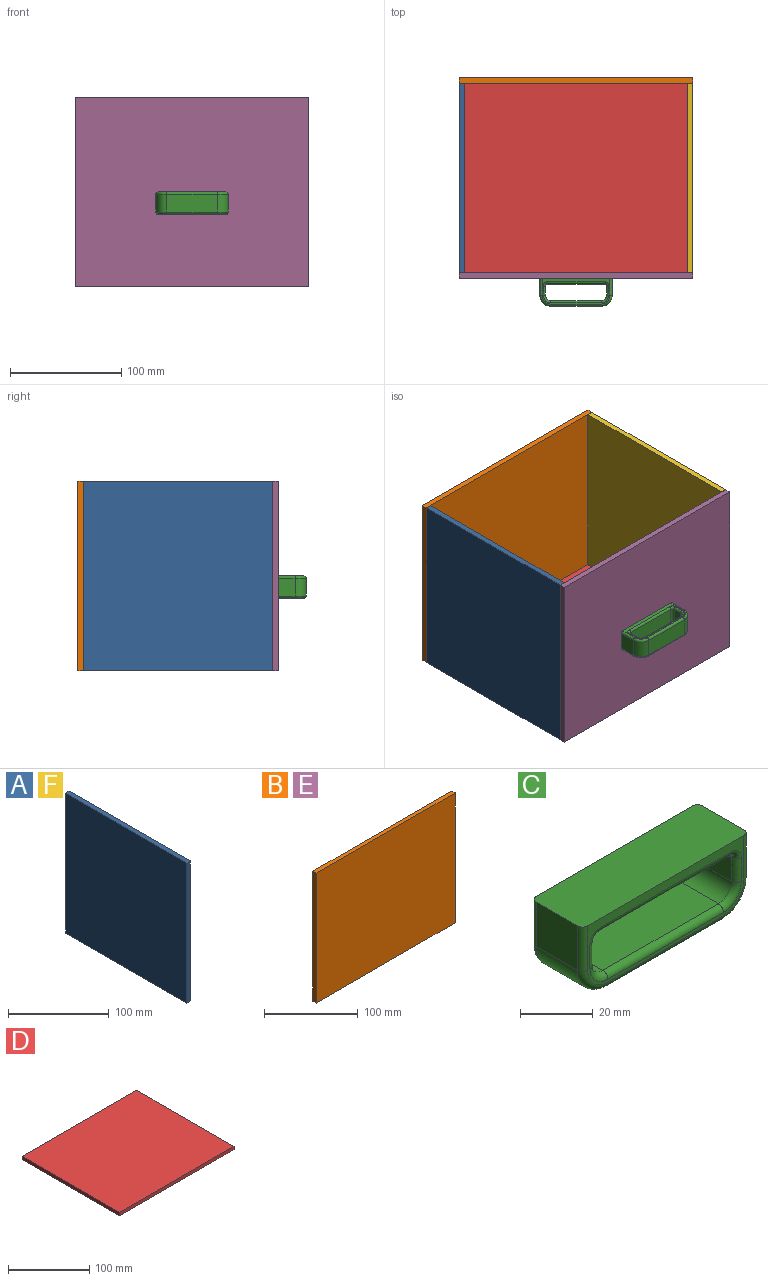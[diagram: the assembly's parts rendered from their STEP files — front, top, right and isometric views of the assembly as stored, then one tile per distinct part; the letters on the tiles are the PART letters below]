
ASSEMBLY  parts=6 mates=13
PART A: 6 faces, bbox 5x170x170 mm
  f0: plane 170x5mm, normal (0,0,1), area 850mm2, adj f1,f3,f4,f5
  f1: plane 170x5mm, normal (0,-1,0), area 850mm2, adj f0,f2,f4,f5
  f2: plane 170x5mm, normal (0,0,-1), area 850mm2, adj f1,f3,f4,f5
  f3: plane 170x5mm, normal (0,1,0), area 850mm2, adj f0,f2,f4,f5
  f4: plane 170x170mm, normal (1,0,0), area 28900mm2, adj f0,f1,f2,f3
  f5: plane 170x170mm, normal (-1,0,0), area 28900mm2, adj f0,f1,f2,f3
PART B: 6 faces, bbox 210x5x170 mm
  f0: plane 210x5mm, normal (0,0,1), area 1050mm2, adj f1,f3,f4,f5
  f1: plane 170x5mm, normal (-1,0,0), area 850mm2, adj f0,f2,f4,f5
  f2: plane 210x5mm, normal (0,0,-1), area 1050mm2, adj f1,f3,f4,f5
  f3: plane 170x5mm, normal (1,0,0), area 850mm2, adj f0,f2,f4,f5
  f4: plane 210x170mm, normal (0,-1,0), area 35700mm2, adj f0,f1,f2,f3
  f5: plane 210x170mm, normal (0,1,0), area 35700mm2, adj f0,f1,f2,f3
PART C: 42 faces, bbox 66.6x20x25.8 mm
  f0: plane 61x23mm, normal (0,1,0), area 282.4mm2, adj f5,f19,f20,f21,f22,f23,f33,f34
  f1: plane 61x23mm, normal (0,-1,0), area 282.4mm2, adj f5,f14,f15,f16,f17,f18,f24,f25
  f2: plane 16x15mm, normal (-1,0,0), area 240mm2, adj f5,f6,f18,f23
  f3: plane 16x15mm, normal (1,0,0), area 240mm2, adj f5,f7,f14,f19
  f4: plane 45x16mm, normal (0,0,-1), area 720mm2, adj f6,f7,f16,f21
  f5: plane 65x20mm, normal (0,0,1), area 1296.6mm2, adj f0,f1,f2,f3,f14,f18,f19,f23
  f6: cylinder r=10mm len=16mm, axis (0,-1,0), area 251.3mm2, adj f2,f4,f17,f22
  f7: cylinder r=10mm len=16mm, axis (0,1,0), area 251.3mm2, adj f3,f4,f15,f20
  f8: plane 16x8mm, normal (1,0,0), area 128mm2, adj f12,f29,f35,f40
  f9: plane 16x8mm, normal (-1,0,0), area 128mm2, adj f13,f26,f31,f34
  f10: plane 45x16mm, normal (0,0,1), area 720mm2, adj f12,f13,f25,f39
  f11: plane 51x16mm, normal (0,0,-1), area 816mm2, adj f30,f31,f35,f36
  f12: cylinder r=5mm len=16mm, axis (0,-1,0), area 125.7mm2, adj f8,f10,f27,f41
  f13: cylinder r=5mm len=16mm, axis (0,1,0), area 125.7mm2, adj f9,f10,f24,f37
  f14: cylinder r=2mm len=15mm, axis (0,0,1), area 47.1mm2, adj f1,f3,f5,f15
  f15: torus R=8mm, axis (0,-1,0), area 45.8mm2, adj f1,f7,f14,f16
  f16: cylinder r=2mm len=45mm, axis (1,0,0), area 141.4mm2, adj f1,f4,f15,f17
  f17: torus R=8mm, axis (0,-1,0), area 45.8mm2, adj f1,f6,f16,f18
  f18: cylinder r=2mm len=15mm, axis (0,0,-1), area 47.1mm2, adj f1,f2,f5,f17
  f19: cylinder r=2mm len=15mm, axis (0,0,-1), area 47.1mm2, adj f0,f3,f5,f20
  f20: torus R=8mm, axis (0,-1,0), area 45.8mm2, adj f0,f7,f19,f21
  f21: cylinder r=2mm len=45mm, axis (-1,0,0), area 141.4mm2, adj f0,f4,f20,f22
  f22: torus R=8mm, axis (0,-1,0), area 45.8mm2, adj f0,f6,f21,f23
  f23: cylinder r=2mm len=15mm, axis (0,0,1), area 47.1mm2, adj f0,f2,f5,f22
  f24: torus R=7mm, axis (0,-1,0), area 28.3mm2, adj f1,f13,f25,f26
  f25: cylinder r=2mm len=45mm, axis (-1,0,0), area 141.4mm2, adj f1,f10,f24,f27
  f26: cylinder r=2mm len=8mm, axis (0,0,-1), area 25.1mm2, adj f1,f9,f24,f28
  f27: torus R=7mm, axis (0,-1,0), area 28.3mm2, adj f1,f12,f25,f29
  f28: torus R=4mm, axis (0,-1,0), area 13.5mm2, adj f1,f26,f30,f31
  f29: cylinder r=2mm len=8mm, axis (0,0,1), area 25.1mm2, adj f1,f8,f27,f32
  f30: cylinder r=2mm len=51mm, axis (1,0,0), area 160.2mm2, adj f1,f11,f28,f32
  f31: cylinder r=2mm len=16mm, axis (0,1,0), area 50.3mm2, adj f9,f11,f28,f33
  f32: torus R=4mm, axis (0,-1,0), area 13.5mm2, adj f1,f29,f30,f35
  f33: torus R=4mm, axis (0,-1,0), area 13.5mm2, adj f0,f31,f34,f36
  f34: cylinder r=2mm len=8mm, axis (0,0,1), area 25.1mm2, adj f0,f9,f33,f37
  f35: cylinder r=2mm len=16mm, axis (0,-1,0), area 50.3mm2, adj f8,f11,f32,f38
  f36: cylinder r=2mm len=51mm, axis (-1,0,0), area 160.2mm2, adj f0,f11,f33,f38
  f37: torus R=7mm, axis (0,-1,0), area 28.3mm2, adj f0,f13,f34,f39
  f38: torus R=4mm, axis (0,-1,0), area 13.5mm2, adj f0,f35,f36,f40
  f39: cylinder r=2mm len=45mm, axis (1,0,0), area 141.4mm2, adj f0,f10,f37,f41
  f40: cylinder r=2mm len=8mm, axis (0,0,-1), area 25.1mm2, adj f0,f8,f38,f41
  f41: torus R=7mm, axis (0,-1,0), area 28.3mm2, adj f0,f12,f39,f40
PART D: 6 faces, bbox 200x170x5 mm
  f0: plane 170x5mm, normal (-1,0,0), area 850mm2, adj f1,f3,f4,f5
  f1: plane 200x5mm, normal (0,-1,0), area 1000mm2, adj f0,f2,f4,f5
  f2: plane 170x5mm, normal (1,0,0), area 850mm2, adj f1,f3,f4,f5
  f3: plane 200x5mm, normal (0,1,0), area 1000mm2, adj f0,f2,f4,f5
  f4: plane 200x170mm, normal (0,0,1), area 34000mm2, adj f0,f1,f2,f3
  f5: plane 200x170mm, normal (0,0,-1), area 34000mm2, adj f0,f1,f2,f3
PART E: same geometry as B
PART F: same geometry as A
PLACE A t=(-252.14,-37.62,53.3)mm
PLACE B t=(-133.3,58.66,6.87)mm
PLACE C rot(axis=(-1,0,0),90deg) t=(-147.14,-116.34,46.28)mm
PLACE D t=(-144.91,-20.6,-28.72)mm
PLACE E t=(-133.3,-116.34,6.87)mm
PLACE F t=(-47.14,-37.62,53.3)mm
MATE planar F.f5 <-> D.f2  axis (-1,0,0) through (-47.14,-31.34,56.28)mm
MATE planar A.f5 <-> E.f1  axis (-1,0,0) through (-252.14,-31.34,56.28)mm
MATE planar A.f4 <-> D.f0  axis (1,0,0) through (-247.14,-31.34,141.28)mm
MATE planar A.f1 <-> E.f5  axis (0,-1,0) through (-249.64,-116.34,56.28)mm
MATE planar D.f1 <-> E.f5  axis (0,-1,0) through (-147.14,-116.34,-26.22)mm
MATE planar D.f5 <-> B.f2  axis (0,0,-1) through (-147.14,-31.34,-28.72)mm
MATE planar D.f5 <-> F.f2  axis (0,0,-1) through (-147.14,-31.34,-28.72)mm
MATE planar F.f1 <-> E.f5  axis (0,-1,0) through (-44.64,-116.34,56.28)mm
MATE planar D.f5 <-> A.f2  axis (0,0,-1) through (-147.14,-31.34,-28.72)mm
MATE planar B.f4 <-> D.f3  axis (0,-1,0) through (-147.14,53.66,-28.72)mm
MATE planar A.f5 <-> B.f1  axis (-1,0,0) through (-252.14,-31.34,56.28)mm
MATE fastened C.f5 <-> E.f4  axis (0,1,0) through (-147.14,-121.34,56.28)mm
MATE planar D.f5 <-> E.f2  axis (0,0,-1) through (-147.14,-116.34,-28.72)mm
